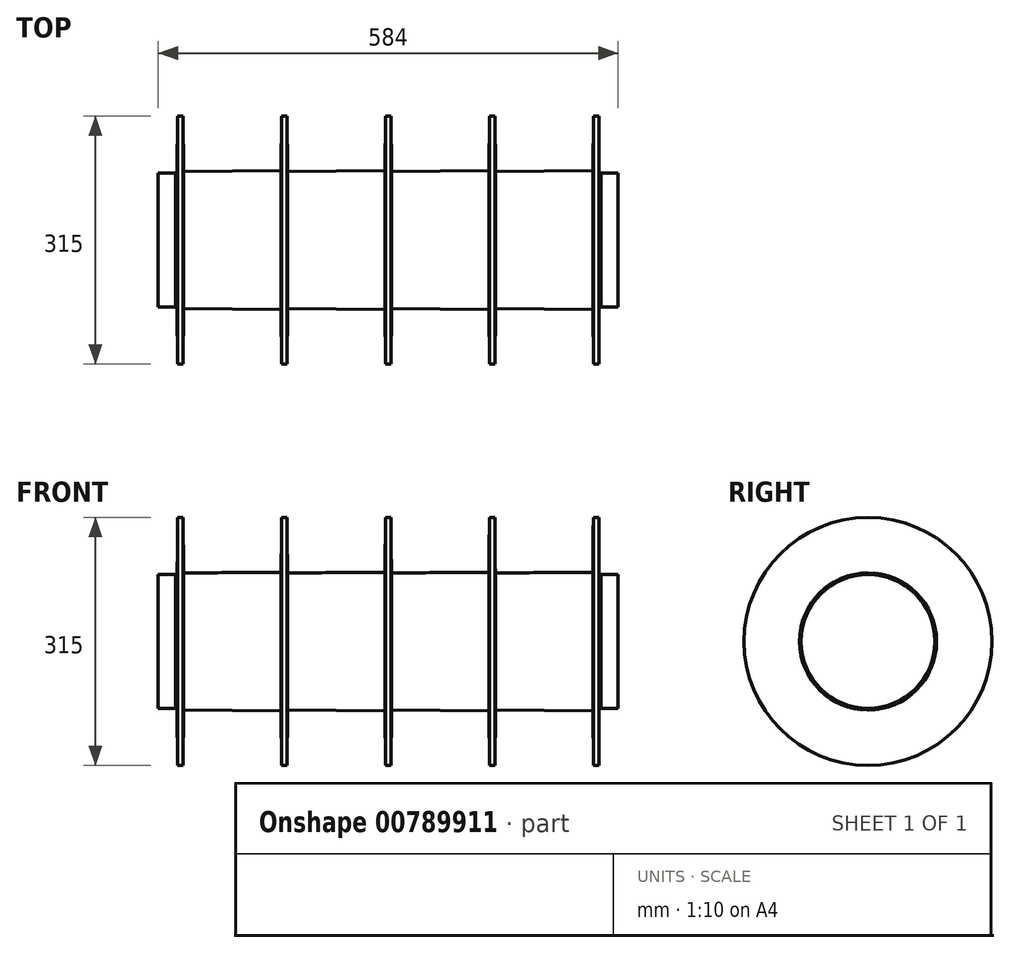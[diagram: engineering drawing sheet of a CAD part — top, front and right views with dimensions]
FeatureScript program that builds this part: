
annotation { "Feature Type Name" : "Feature", "Feature Type Description" : "" }
export const myFeature = defineFeature(function(context is Context, id is Id, definition is map)
    precondition{}
    {
        {
            var Q0;
            Q0=qCreatedBy(makeId("Front.planeOp"),FACE);
            var sketch = newSketch(context, id + "F0", { "sketchPlane" : qUnion([Q0])});
            skLineSegment(sketch, "E0", {"start": v(-271.12, 30.89) * mm, "end": v(-262.12, 30.89) * mm, "construction": true});
            skLineSegment(sketch, "E1", {"start": v(0, -78.9) * mm, "end": v(0, 78.9) * mm, "construction": true});
            skLineSegment(sketch, "E2", {"start": v(1.78, -78.9) * mm, "end": v(3.9, -78.9) * mm, "construction": true});
            skLineSegment(sketch, "E3", {"start": v(1.78, 78.9) * mm, "end": v(3.9, 78.9) * mm, "construction": true});
            skLineSegment(sketch, "E4", {"start": v(266.88, 30.89) * mm, "end": v(257.88, 30.89) * mm, "construction": true});
            skLineSegment(sketch, "E5", {"start": v(298.88, 30.89) * mm, "end": v(307.88, 30.89) * mm, "construction": true});
            skLineSegment(sketch, "E6", {"start": v(-138.11, -88) * mm, "end": v(-139.47, -88) * mm, "construction": true});
            skLineSegment(sketch, "E7", {"start": v(-144.77, -88) * mm, "end": v(-147.47, -88) * mm, "construction": true});
            skLineSegment(sketch, "E8", {"start": v(-176.77, -88) * mm, "end": v(-179.47, -88) * mm, "construction": true});
            skLineSegment(sketch, "E9", {"start": v(-168.77, -88) * mm, "end": v(-171.47, -88) * mm, "construction": true});
            skLineSegment(sketch, "E10", {"start": v(-152.77, -88) * mm, "end": v(-155.47, -88) * mm, "construction": true});
            skLineSegment(sketch, "E11", {"start": v(-160.77, -88) * mm, "end": v(-163.47, -88) * mm, "construction": true});
            skLineSegment(sketch, "E12", {"start": v(-192.77, -88) * mm, "end": v(-195.47, -88) * mm, "construction": true});
            skLineSegment(sketch, "E13", {"start": v(-208.77, -88) * mm, "end": v(-211.47, -88) * mm, "construction": true});
            skLineSegment(sketch, "E14", {"start": v(-200.77, -88) * mm, "end": v(-203.47, -88) * mm, "construction": true});
            skLineSegment(sketch, "E15", {"start": v(-184.77, -88) * mm, "end": v(-187.47, -88) * mm, "construction": true});
            skLineSegment(sketch, "E16", {"start": v(-224.77, -88) * mm, "end": v(-227.47, -88) * mm, "construction": true});
            skLineSegment(sketch, "E17", {"start": v(-240.77, -88) * mm, "end": v(-243.47, -88) * mm, "construction": true});
            skLineSegment(sketch, "E18", {"start": v(-232.77, -88) * mm, "end": v(-235.47, -88) * mm, "construction": true});
            skLineSegment(sketch, "E19", {"start": v(-216.77, -88) * mm, "end": v(-219.47, -88) * mm, "construction": true});
            skLineSegment(sketch, "E20", {"start": v(-256.77, -88) * mm, "end": v(-259.47, -88) * mm, "construction": true});
            skLineSegment(sketch, "E21", {"start": v(-248.77, -88) * mm, "end": v(-251.47, -88) * mm, "construction": true});
            skLineSegment(sketch, "E22", {"start": v(-269.62, -157.5) * mm, "end": v(-262.62, -157.5) * mm, "construction": true});
            skLineSegment(sketch, "E23", {"start": v(275.88, -78.9) * mm, "end": v(-280.12, -78.9) * mm, "construction": true});
            skLineSegment(sketch, "E24", {"start": v(284.33, 0) * mm, "end": v(-280.12, 0) * mm, "construction": true});
            skLineSegment(sketch, "E25", {"start": v(-270.12, -87) * mm, "end": v(-272.12, -87) * mm, "construction": true});
            skLineSegment(sketch, "E26", {"start": v(-270.12, -87) * mm, "end": v(-269.62, -157.5) * mm, "construction": true});
            skLineSegment(sketch, "E27", {"start": v(-262.12, -87) * mm, "end": v(-262.62, -157.5) * mm, "construction": true});
            skLineSegment(sketch, "E28", {"start": v(-130.12, -87) * mm, "end": v(-130.62, -157.5) * mm, "construction": true});
            skLineSegment(sketch, "E29", {"start": v(-138.11, -88) * mm, "end": v(-137.62, -157.5) * mm, "construction": true});
            skLineSegment(sketch, "E30", {"start": v(-137.62, -157.5) * mm, "end": v(-130.62, -157.5) * mm, "construction": true});
            skLineSegment(sketch, "E31", {"start": v(-5.62, -157.5) * mm, "end": v(1.38, -157.5) * mm, "construction": true});
            skLineSegment(sketch, "E32", {"start": v(-6.11, -88) * mm, "end": v(-5.62, -157.5) * mm, "construction": true});
            skLineSegment(sketch, "E33", {"start": v(1.88, -87) * mm, "end": v(1.38, -157.5) * mm, "construction": true});
            skLineSegment(sketch, "E34", {"start": v(-116.77, -88) * mm, "end": v(-119.47, -88) * mm, "construction": true});
            skLineSegment(sketch, "E35", {"start": v(-124.77, -88) * mm, "end": v(-127.47, -88) * mm, "construction": true});
            skLineSegment(sketch, "E36", {"start": v(-84.77, -88) * mm, "end": v(-87.47, -88) * mm, "construction": true});
            skLineSegment(sketch, "E37", {"start": v(-100.77, -88) * mm, "end": v(-103.47, -88) * mm, "construction": true});
            skLineSegment(sketch, "E38", {"start": v(-108.77, -88) * mm, "end": v(-111.47, -88) * mm, "construction": true});
            skLineSegment(sketch, "E39", {"start": v(-92.77, -88) * mm, "end": v(-95.47, -88) * mm, "construction": true});
            skLineSegment(sketch, "E40", {"start": v(-52.77, -88) * mm, "end": v(-55.47, -88) * mm, "construction": true});
            skLineSegment(sketch, "E41", {"start": v(-68.77, -88) * mm, "end": v(-71.47, -88) * mm, "construction": true});
            skLineSegment(sketch, "E42", {"start": v(-76.77, -88) * mm, "end": v(-79.47, -88) * mm, "construction": true});
            skLineSegment(sketch, "E43", {"start": v(-60.77, -88) * mm, "end": v(-63.47, -88) * mm, "construction": true});
            skLineSegment(sketch, "E44", {"start": v(-28.77, -88) * mm, "end": v(-31.47, -88) * mm, "construction": true});
            skLineSegment(sketch, "E45", {"start": v(-20.77, -88) * mm, "end": v(-23.47, -88) * mm, "construction": true});
            skLineSegment(sketch, "E46", {"start": v(-36.77, -88) * mm, "end": v(-39.47, -88) * mm, "construction": true});
            skLineSegment(sketch, "E47", {"start": v(-44.77, -88) * mm, "end": v(-47.47, -88) * mm, "construction": true});
            skLineSegment(sketch, "E48", {"start": v(-12.77, -88) * mm, "end": v(-15.47, -88) * mm, "construction": true});
            skLineSegment(sketch, "E49", {"start": v(-6.11, -88) * mm, "end": v(-7.47, -88) * mm, "construction": true});
            skLineSegment(sketch, "E50", {"start": v(126.38, -157.5) * mm, "end": v(133.38, -157.5) * mm, "construction": true});
            skLineSegment(sketch, "E51", {"start": v(125.89, -88) * mm, "end": v(126.38, -157.5) * mm, "construction": true});
            skLineSegment(sketch, "E52", {"start": v(133.88, -87) * mm, "end": v(133.38, -157.5) * mm, "construction": true});
            skLineSegment(sketch, "E53", {"start": v(15.23, -88) * mm, "end": v(12.53, -88) * mm, "construction": true});
            skLineSegment(sketch, "E54", {"start": v(7.23, -88) * mm, "end": v(4.53, -88) * mm, "construction": true});
            skLineSegment(sketch, "E55", {"start": v(47.23, -88) * mm, "end": v(44.53, -88) * mm, "construction": true});
            skLineSegment(sketch, "E56", {"start": v(31.23, -88) * mm, "end": v(28.53, -88) * mm, "construction": true});
            skLineSegment(sketch, "E57", {"start": v(23.23, -88) * mm, "end": v(20.53, -88) * mm, "construction": true});
            skLineSegment(sketch, "E58", {"start": v(39.23, -88) * mm, "end": v(36.53, -88) * mm, "construction": true});
            skLineSegment(sketch, "E59", {"start": v(79.23, -88) * mm, "end": v(76.53, -88) * mm, "construction": true});
            skLineSegment(sketch, "E60", {"start": v(63.23, -88) * mm, "end": v(60.53, -88) * mm, "construction": true});
            skLineSegment(sketch, "E61", {"start": v(55.23, -88) * mm, "end": v(52.53, -88) * mm, "construction": true});
            skLineSegment(sketch, "E62", {"start": v(71.23, -88) * mm, "end": v(68.53, -88) * mm, "construction": true});
            skLineSegment(sketch, "E63", {"start": v(103.23, -88) * mm, "end": v(100.53, -88) * mm, "construction": true});
            skLineSegment(sketch, "E64", {"start": v(111.23, -88) * mm, "end": v(108.53, -88) * mm, "construction": true});
            skLineSegment(sketch, "E65", {"start": v(95.23, -88) * mm, "end": v(92.53, -88) * mm, "construction": true});
            skLineSegment(sketch, "E66", {"start": v(87.23, -88) * mm, "end": v(84.53, -88) * mm, "construction": true});
            skLineSegment(sketch, "E67", {"start": v(119.23, -88) * mm, "end": v(116.53, -88) * mm, "construction": true});
            skLineSegment(sketch, "E68", {"start": v(125.89, -88) * mm, "end": v(124.53, -88) * mm, "construction": true});
            skLineSegment(sketch, "E69", {"start": v(258.38, -157.5) * mm, "end": v(265.38, -157.5) * mm, "construction": true});
            skLineSegment(sketch, "E70", {"start": v(257.89, -88) * mm, "end": v(258.38, -157.5) * mm, "construction": true});
            skLineSegment(sketch, "E71", {"start": v(265.88, -87) * mm, "end": v(265.38, -157.5) * mm, "construction": true});
            skLineSegment(sketch, "E72", {"start": v(147.23, -88) * mm, "end": v(144.53, -88) * mm, "construction": true});
            skLineSegment(sketch, "E73", {"start": v(139.23, -88) * mm, "end": v(136.53, -88) * mm, "construction": true});
            skLineSegment(sketch, "E74", {"start": v(179.23, -88) * mm, "end": v(176.53, -88) * mm, "construction": true});
            skLineSegment(sketch, "E75", {"start": v(163.23, -88) * mm, "end": v(160.53, -88) * mm, "construction": true});
            skLineSegment(sketch, "E76", {"start": v(155.23, -88) * mm, "end": v(152.53, -88) * mm, "construction": true});
            skLineSegment(sketch, "E77", {"start": v(171.23, -88) * mm, "end": v(168.53, -88) * mm, "construction": true});
            skLineSegment(sketch, "E78", {"start": v(211.23, -88) * mm, "end": v(208.53, -88) * mm, "construction": true});
            skLineSegment(sketch, "E79", {"start": v(195.23, -88) * mm, "end": v(192.53, -88) * mm, "construction": true});
            skLineSegment(sketch, "E80", {"start": v(187.23, -88) * mm, "end": v(184.53, -88) * mm, "construction": true});
            skLineSegment(sketch, "E81", {"start": v(203.23, -88) * mm, "end": v(200.53, -88) * mm, "construction": true});
            skLineSegment(sketch, "E82", {"start": v(235.23, -88) * mm, "end": v(232.53, -88) * mm, "construction": true});
            skLineSegment(sketch, "E83", {"start": v(243.23, -88) * mm, "end": v(240.53, -88) * mm, "construction": true});
            skLineSegment(sketch, "E84", {"start": v(227.23, -88) * mm, "end": v(224.53, -88) * mm, "construction": true});
            skLineSegment(sketch, "E85", {"start": v(219.23, -88) * mm, "end": v(216.53, -88) * mm, "construction": true});
            skLineSegment(sketch, "E86", {"start": v(251.23, -88) * mm, "end": v(248.53, -88) * mm, "construction": true});
            skLineSegment(sketch, "E87", {"start": v(257.89, -88) * mm, "end": v(256.53, -88) * mm, "construction": true});
            skLineSegment(sketch, "E88", {"start": v(275.88, -78.9) * mm, "end": v(275.88, 0) * mm, "construction": true});
            skLineSegment(sketch, "E89", {"start": v(265.88, -87) * mm, "end": v(267.88, -87) * mm, "construction": true});
            skLineSegment(sketch, "E90", {"start": v(265.88, 87) * mm, "end": v(267.88, 87) * mm, "construction": true});
            skLineSegment(sketch, "E91", {"start": v(257.89, 88) * mm, "end": v(256.53, 88) * mm, "construction": true});
            skLineSegment(sketch, "E92", {"start": v(251.23, 88) * mm, "end": v(248.53, 88) * mm, "construction": true});
            skLineSegment(sketch, "E93", {"start": v(219.23, 88) * mm, "end": v(216.53, 88) * mm, "construction": true});
            skLineSegment(sketch, "E94", {"start": v(227.23, 88) * mm, "end": v(224.53, 88) * mm, "construction": true});
            skLineSegment(sketch, "E95", {"start": v(243.23, 88) * mm, "end": v(240.53, 88) * mm, "construction": true});
            skLineSegment(sketch, "E96", {"start": v(235.23, 88) * mm, "end": v(232.53, 88) * mm, "construction": true});
            skLineSegment(sketch, "E97", {"start": v(203.23, 88) * mm, "end": v(200.53, 88) * mm, "construction": true});
            skLineSegment(sketch, "E98", {"start": v(187.23, 88) * mm, "end": v(184.53, 88) * mm, "construction": true});
            skLineSegment(sketch, "E99", {"start": v(195.23, 88) * mm, "end": v(192.53, 88) * mm, "construction": true});
            skLineSegment(sketch, "E100", {"start": v(211.23, 88) * mm, "end": v(208.53, 88) * mm, "construction": true});
            skLineSegment(sketch, "E101", {"start": v(171.23, 88) * mm, "end": v(168.53, 88) * mm, "construction": true});
            skLineSegment(sketch, "E102", {"start": v(155.23, 88) * mm, "end": v(152.53, 88) * mm, "construction": true});
            skLineSegment(sketch, "E103", {"start": v(163.23, 88) * mm, "end": v(160.53, 88) * mm, "construction": true});
            skLineSegment(sketch, "E104", {"start": v(179.23, 88) * mm, "end": v(176.53, 88) * mm, "construction": true});
            skLineSegment(sketch, "E105", {"start": v(139.23, 88) * mm, "end": v(136.53, 88) * mm, "construction": true});
            skLineSegment(sketch, "E106", {"start": v(147.23, 88) * mm, "end": v(144.53, 88) * mm, "construction": true});
            skLineSegment(sketch, "E107", {"start": v(265.88, 87) * mm, "end": v(265.38, 157.5) * mm});
            skLineSegment(sketch, "E108", {"start": v(257.89, 88) * mm, "end": v(258.38, 157.5) * mm});
            skLineSegment(sketch, "E109", {"start": v(258.38, 157.5) * mm, "end": v(265.38, 157.5) * mm});
            skLineSegment(sketch, "E110", {"start": v(125.89, 88) * mm, "end": v(124.53, 88) * mm, "construction": true});
            skLineSegment(sketch, "E111", {"start": v(119.23, 88) * mm, "end": v(116.53, 88) * mm, "construction": true});
            skLineSegment(sketch, "E112", {"start": v(87.23, 88) * mm, "end": v(84.53, 88) * mm, "construction": true});
            skLineSegment(sketch, "E113", {"start": v(95.23, 88) * mm, "end": v(92.53, 88) * mm, "construction": true});
            skLineSegment(sketch, "E114", {"start": v(111.23, 88) * mm, "end": v(108.53, 88) * mm, "construction": true});
            skLineSegment(sketch, "E115", {"start": v(103.23, 88) * mm, "end": v(100.53, 88) * mm, "construction": true});
            skLineSegment(sketch, "E116", {"start": v(71.23, 88) * mm, "end": v(68.53, 88) * mm, "construction": true});
            skLineSegment(sketch, "E117", {"start": v(55.23, 88) * mm, "end": v(52.53, 88) * mm, "construction": true});
            skLineSegment(sketch, "E118", {"start": v(63.23, 88) * mm, "end": v(60.53, 88) * mm, "construction": true});
            skLineSegment(sketch, "E119", {"start": v(79.23, 88) * mm, "end": v(76.53, 88) * mm, "construction": true});
            skLineSegment(sketch, "E120", {"start": v(39.23, 88) * mm, "end": v(36.53, 88) * mm, "construction": true});
            skLineSegment(sketch, "E121", {"start": v(23.23, 88) * mm, "end": v(20.53, 88) * mm, "construction": true});
            skLineSegment(sketch, "E122", {"start": v(31.23, 88) * mm, "end": v(28.53, 88) * mm, "construction": true});
            skLineSegment(sketch, "E123", {"start": v(47.23, 88) * mm, "end": v(44.53, 88) * mm, "construction": true});
            skLineSegment(sketch, "E124", {"start": v(7.23, 88) * mm, "end": v(4.53, 88) * mm, "construction": true});
            skLineSegment(sketch, "E125", {"start": v(15.23, 88) * mm, "end": v(12.53, 88) * mm, "construction": true});
            skLineSegment(sketch, "E126", {"start": v(133.88, 87) * mm, "end": v(133.38, 157.5) * mm});
            skLineSegment(sketch, "E127", {"start": v(125.89, 88) * mm, "end": v(126.38, 157.5) * mm});
            skLineSegment(sketch, "E128", {"start": v(126.38, 157.5) * mm, "end": v(133.38, 157.5) * mm});
            skLineSegment(sketch, "E129", {"start": v(-6.11, 88) * mm, "end": v(-7.47, 88) * mm, "construction": true});
            skLineSegment(sketch, "E130", {"start": v(-12.77, 88) * mm, "end": v(-15.47, 88) * mm, "construction": true});
            skLineSegment(sketch, "E131", {"start": v(-44.77, 88) * mm, "end": v(-47.47, 88) * mm, "construction": true});
            skLineSegment(sketch, "E132", {"start": v(-36.77, 88) * mm, "end": v(-39.47, 88) * mm, "construction": true});
            skLineSegment(sketch, "E133", {"start": v(-20.77, 88) * mm, "end": v(-23.47, 88) * mm, "construction": true});
            skLineSegment(sketch, "E134", {"start": v(-28.77, 88) * mm, "end": v(-31.47, 88) * mm, "construction": true});
            skLineSegment(sketch, "E135", {"start": v(-60.77, 88) * mm, "end": v(-63.47, 88) * mm, "construction": true});
            skLineSegment(sketch, "E136", {"start": v(-76.77, 88) * mm, "end": v(-79.47, 88) * mm, "construction": true});
            skLineSegment(sketch, "E137", {"start": v(-68.77, 88) * mm, "end": v(-71.47, 88) * mm, "construction": true});
            skLineSegment(sketch, "E138", {"start": v(-52.77, 88) * mm, "end": v(-55.47, 88) * mm, "construction": true});
            skLineSegment(sketch, "E139", {"start": v(-92.77, 88) * mm, "end": v(-95.47, 88) * mm, "construction": true});
            skLineSegment(sketch, "E140", {"start": v(-108.77, 88) * mm, "end": v(-111.47, 88) * mm, "construction": true});
            skLineSegment(sketch, "E141", {"start": v(-100.77, 88) * mm, "end": v(-103.47, 88) * mm, "construction": true});
            skLineSegment(sketch, "E142", {"start": v(-84.77, 88) * mm, "end": v(-87.47, 88) * mm, "construction": true});
            skLineSegment(sketch, "E143", {"start": v(-124.77, 88) * mm, "end": v(-127.47, 88) * mm, "construction": true});
            skLineSegment(sketch, "E144", {"start": v(-116.77, 88) * mm, "end": v(-119.47, 88) * mm, "construction": true});
            skLineSegment(sketch, "E145", {"start": v(1.88, 87) * mm, "end": v(1.38, 157.5) * mm});
            skLineSegment(sketch, "E146", {"start": v(-6.11, 88) * mm, "end": v(-5.62, 157.5) * mm});
            skLineSegment(sketch, "E147", {"start": v(-5.62, 157.5) * mm, "end": v(1.38, 157.5) * mm});
            skLineSegment(sketch, "E148", {"start": v(-137.62, 157.5) * mm, "end": v(-130.62, 157.5) * mm});
            skLineSegment(sketch, "E149", {"start": v(-138.11, 88) * mm, "end": v(-137.62, 157.5) * mm});
            skLineSegment(sketch, "E150", {"start": v(-130.12, 87) * mm, "end": v(-130.62, 157.5) * mm});
            skLineSegment(sketch, "E151", {"start": v(-262.12, 87) * mm, "end": v(-262.62, 157.5) * mm});
            skLineSegment(sketch, "E152", {"start": v(-270.12, 87) * mm, "end": v(-269.62, 157.5) * mm});
            skLineSegment(sketch, "E153", {"start": v(-270.12, 87) * mm, "end": v(-272.12, 87) * mm, "construction": true});
            skLineSegment(sketch, "E154", {"start": v(275.88, 78.9) * mm, "end": v(-280.12, 78.9) * mm, "construction": true});
            skLineSegment(sketch, "E155", {"start": v(-269.62, 157.5) * mm, "end": v(-262.62, 157.5) * mm});
            skLineSegment(sketch, "E156", {"start": v(-248.77, 88) * mm, "end": v(-251.47, 88) * mm, "construction": true});
            skLineSegment(sketch, "E157", {"start": v(-256.77, 88) * mm, "end": v(-259.47, 88) * mm, "construction": true});
            skLineSegment(sketch, "E158", {"start": v(-216.77, 88) * mm, "end": v(-219.47, 88) * mm, "construction": true});
            skLineSegment(sketch, "E159", {"start": v(-232.77, 88) * mm, "end": v(-235.47, 88) * mm, "construction": true});
            skLineSegment(sketch, "E160", {"start": v(-240.77, 88) * mm, "end": v(-243.47, 88) * mm, "construction": true});
            skLineSegment(sketch, "E161", {"start": v(-224.77, 88) * mm, "end": v(-227.47, 88) * mm, "construction": true});
            skLineSegment(sketch, "E162", {"start": v(-184.77, 88) * mm, "end": v(-187.47, 88) * mm, "construction": true});
            skLineSegment(sketch, "E163", {"start": v(-200.77, 88) * mm, "end": v(-203.47, 88) * mm, "construction": true});
            skLineSegment(sketch, "E164", {"start": v(-208.77, 88) * mm, "end": v(-211.47, 88) * mm, "construction": true});
            skLineSegment(sketch, "E165", {"start": v(-192.77, 88) * mm, "end": v(-195.47, 88) * mm, "construction": true});
            skLineSegment(sketch, "E166", {"start": v(-160.77, 88) * mm, "end": v(-163.47, 88) * mm, "construction": true});
            skLineSegment(sketch, "E167", {"start": v(-152.77, 88) * mm, "end": v(-155.47, 88) * mm, "construction": true});
            skLineSegment(sketch, "E168", {"start": v(-168.77, 88) * mm, "end": v(-171.47, 88) * mm, "construction": true});
            skLineSegment(sketch, "E169", {"start": v(-176.77, 88) * mm, "end": v(-179.47, 88) * mm, "construction": true});
            skLineSegment(sketch, "E170", {"start": v(-144.77, 88) * mm, "end": v(-147.47, 88) * mm, "construction": true});
            skLineSegment(sketch, "E171", {"start": v(-138.11, 88) * mm, "end": v(-139.47, 88) * mm, "construction": true});
            skLineSegment(sketch, "E172", {"start": v(-272.12, 87) * mm, "end": v(-272.12, 85) * mm, "construction": true});
            skLineSegment(sketch, "E173", {"start": v(-272.12, 85) * mm, "end": v(-294.12, 85) * mm, "construction": true});
            skLineSegment(sketch, "E174", {"start": v(-294.12, -85) * mm, "end": v(-272.12, -85) * mm, "construction": true});
            skLineSegment(sketch, "E175", {"start": v(-272.12, -85) * mm, "end": v(-272.12, -87) * mm, "construction": true});
            skLineSegment(sketch, "E176", {"start": v(-280.12, -45) * mm, "end": v(-294.12, -45) * mm, "construction": true});
            skLineSegment(sketch, "E177", {"start": v(267.88, 87) * mm, "end": v(267.88, 85) * mm, "construction": true});
            skLineSegment(sketch, "E178", {"start": v(267.88, 85) * mm, "end": v(289.88, 85) * mm, "construction": true});
            skLineSegment(sketch, "E179", {"start": v(289.88, -85) * mm, "end": v(267.88, -85) * mm, "construction": true});
            skLineSegment(sketch, "E180", {"start": v(267.88, -85) * mm, "end": v(267.88, -87) * mm, "construction": true});
            skLineSegment(sketch, "E181", {"start": v(275.88, -45) * mm, "end": v(289.88, -45) * mm, "construction": true});
            skCircle(sketch, "E182", {"center": v(416.84, 0) * mm, "radius": 78.9 * mm, "construction": true});
            skLineSegment(sketch, "E183", {"start": v(486.21, 67.71) * mm, "end": v(477.21, 67.71) * mm, "construction": true});
            skCircle(sketch, "E184", {"center": v(473.9, 18.54) * mm, "radius": 6 * mm, "construction": true});
            skLineSegment(sketch, "E185", {"start": v(477.21, 67.71) * mm, "end": v(462.76, 51.5) * mm, "construction": true});
            skCircle(sketch, "E186", {"center": v(416.84, 60) * mm, "radius": 6 * mm, "construction": true});
            skLineSegment(sketch, "E187", {"start": v(331.58, 68.2) * mm, "end": v(340.58, 68.2) * mm, "construction": true});
            skCircle(sketch, "E188", {"center": v(359.78, 18.54) * mm, "radius": 6 * mm, "construction": true});
            skLineSegment(sketch, "E189", {"start": v(340.58, 68.2) * mm, "end": v(376.6, 36) * mm, "construction": true});
            skCircle(sketch, "E190", {"center": v(381.58, -48.54) * mm, "radius": 6 * mm, "construction": true});
            skLineSegment(sketch, "E191", {"start": v(353.8, -71.33) * mm, "end": v(369.98, -58.06) * mm, "construction": true});
            skCircle(sketch, "E192", {"center": v(452.1, -48.54) * mm, "radius": 6 * mm, "construction": true});
            skCircle(sketch, "E193", {"center": v(416.84, 0) * mm, "radius": 85 * mm, "construction": true});
            skCircle(sketch, "E194", {"center": v(416.84, 0) * mm, "radius": 45 * mm, "construction": true});
            skCircle(sketch, "E195", {"center": v(416.84, 0) * mm, "radius": 60 * mm, "construction": true});
            skLineSegment(sketch, "E196", {"start": v(267.88, 85) * mm, "end": v(265.88, 87) * mm, "construction": true});
            skLineSegment(sketch, "E197", {"start": v(267.88, 85) * mm, "end": v(265.88, 87) * mm});
            skLineSegment(sketch, "E198", {"start": v(257.89, 88) * mm, "end": v(133.88, 87) * mm});
            skLineSegment(sketch, "E199", {"start": v(125.89, 88) * mm, "end": v(1.88, 87) * mm});
            skLineSegment(sketch, "E200", {"start": v(-6.11, 88) * mm, "end": v(-130.12, 87) * mm});
            skLineSegment(sketch, "E201", {"start": v(-138.11, 88) * mm, "end": v(-262.12, 87) * mm});
            skLineSegment(sketch, "E202", {"start": v(-270.12, 87) * mm, "end": v(-272.12, 85) * mm});
            skLineSegment(sketch, "E203", {"start": v(-272.12, 85) * mm, "end": v(-294.12, 85) * mm});
            skLineSegment(sketch, "E204", {"start": v(-294.12, 85) * mm, "end": v(-294.12, 0) * mm});
            skLineSegment(sketch, "E205", {"start": v(-294.12, 0) * mm, "end": v(289.88, 0) * mm});
            skLineSegment(sketch, "E206", {"start": v(267.88, 85) * mm, "end": v(289.88, 85) * mm});
            skLineSegment(sketch, "E207", {"start": v(289.88, 0) * mm, "end": v(289.88, 85) * mm});
            skSolve(sketch);
        }
        {
            var Q0;
            Q0=makeQuery(id+"F0.imprint","IMPRINT",FACE,{"disambiguationData":[TD([[makeQuery(id+"F0.imprint","IMPRINT",EDGE,{"derivedFrom":sQuery(id+"F0.wireOp",EDGE,"E107")}),1.0]])]});
            var Q1;
            Q1=sQuery(id+"F0.wireOp",EDGE,"E205");
            revolve(context, id + "F1", {"entities" : qUnion([Q0]), "axis" : qUnion([Q1]), "revolveType" : RevolveType.FULL});
        }
    });
